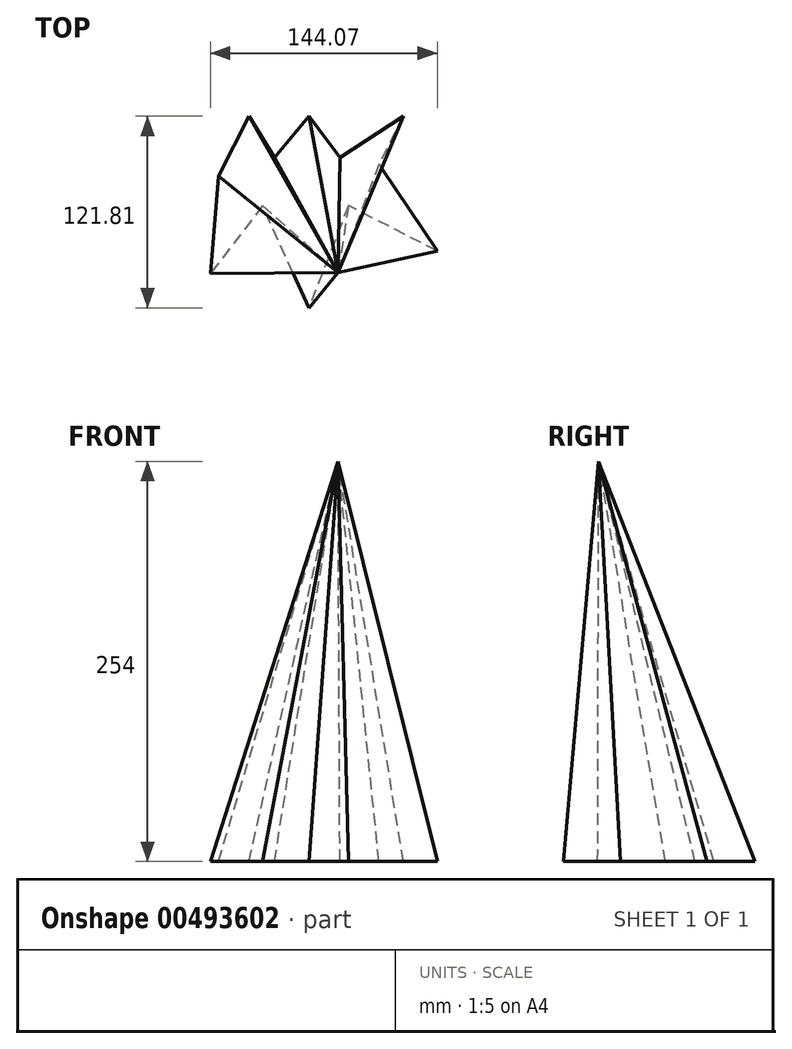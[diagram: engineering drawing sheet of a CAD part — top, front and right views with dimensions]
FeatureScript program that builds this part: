
annotation { "Feature Type Name" : "Feature", "Feature Type Description" : "" }
export const myFeature = defineFeature(function(context is Context, id is Id, definition is map)
    precondition{}
    {
        {
            var Q0;
            Q0=qCreatedBy(makeId("Top.planeOp"),FACE);
            var sketch = newSketch(context, id + "F0", { "sketchPlane" : qUnion([Q0])});
            skLineSegment(sketch, "E0", {"start": v(-67.12, 9.7) * mm, "end": v(-47.69, 47.8) * mm});
            skLineSegment(sketch, "E1", {"start": v(-47.69, 47.8) * mm, "end": v(-31.56, 21.65) * mm});
            skLineSegment(sketch, "E2", {"start": v(-31.56, 21.65) * mm, "end": v(-9.73, 47.8) * mm});
            skLineSegment(sketch, "E3", {"start": v(-9.73, 47.8) * mm, "end": v(9.99, 21.65) * mm});
            skLineSegment(sketch, "E4", {"start": v(9.99, 21.65) * mm, "end": v(50.35, 47.8) * mm});
            skLineSegment(sketch, "E5", {"start": v(50.35, 47.8) * mm, "end": v(34.82, 17.36) * mm});
            skLineSegment(sketch, "E6", {"start": v(34.82, 17.36) * mm, "end": v(71.84, -37.8) * mm});
            skLineSegment(sketch, "E7", {"start": v(71.84, -37.8) * mm, "end": v(15.48, -9.05) * mm});
            skLineSegment(sketch, "E8", {"start": v(15.48, -9.05) * mm, "end": v(-9.77, -74) * mm});
            skLineSegment(sketch, "E9", {"start": v(-9.77, -74) * mm, "end": v(-39.04, -9.05) * mm});
            skLineSegment(sketch, "E10", {"start": v(-39.04, -9.05) * mm, "end": v(-72.23, -52.1) * mm});
            skLineSegment(sketch, "E11", {"start": v(-72.23, -52.1) * mm, "end": v(-67.12, 9.7) * mm});
            skSolve(sketch);
        }
        {
            var Q0;
            Q0=qCreatedBy(makeId("Top.planeOp"),FACE);
            cPlane(context, id + "F1", {"entities" : qUnion([Q0]), "cplaneType" : CPlaneType.OFFSET, "offset" : 254 * mm, "width" : 150 * mm, "height" : 150 * mm});
        }
        {
            var Q0;
            Q0=qCreatedBy(id+"F1.planeOp",FACE);
            var sketch = newSketch(context, id + "F2", { "sketchPlane" : qUnion([Q0])});
            skPoint(sketch, "E12", {"position": v(8.83, -51.5) * mm});
            skSolve(sketch);
        }
        {
            var Q0;
            Q0=makeQuery(id+"F0.imprint","IMPRINT",FACE,{"disambiguationData":[TD([[makeQuery(id+"F0.imprint","IMPRINT",EDGE,{"derivedFrom":sQuery(id+"F0.wireOp",EDGE,"E0")}),-1.0]])]});
            var Q1;
            Q1=sQuery(id+"F2.wireOp",VERTEX,"E12");
            loft(context, id + "F3", {"sheetProfilesArray" : [{ "sheetProfileEntities" : qUnion([Q0]) }, { "sheetProfileEntities" : qUnion([Q1]) }]});
        }
    });
